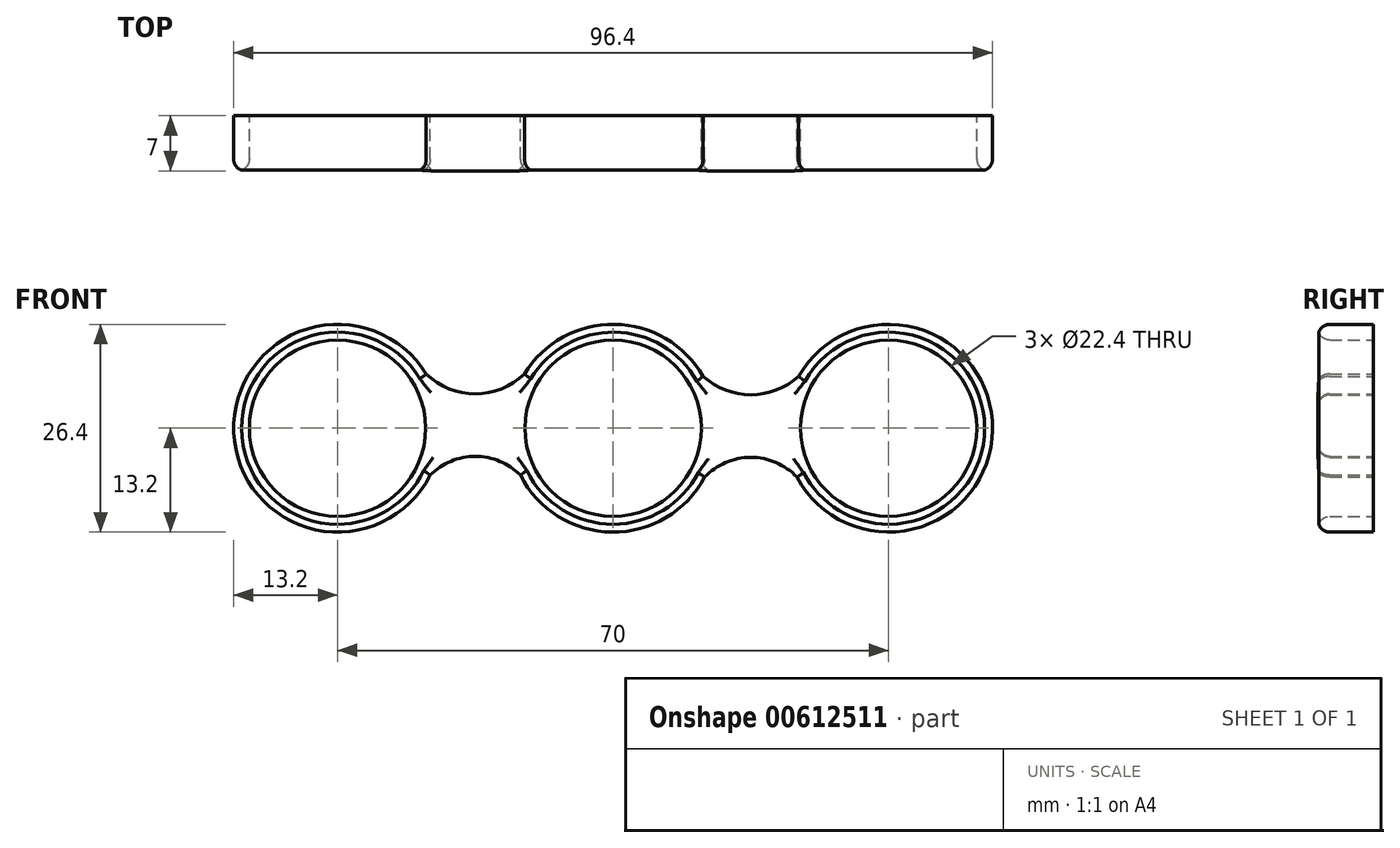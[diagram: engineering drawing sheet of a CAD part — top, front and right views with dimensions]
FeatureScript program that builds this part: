
annotation { "Feature Type Name" : "Feature", "Feature Type Description" : "" }
export const myFeature = defineFeature(function(context is Context, id is Id, definition is map)
    precondition{}
    {
        {
            var Q0;
            Q0=qCreatedBy(makeId("Front.planeOp"),FACE);
            var sketch = newSketch(context, id + "F0", { "sketchPlane" : qUnion([Q0])});
            skCircle(sketch, "E0", {"center": v(0, 0) * mm, "radius": 11.2 * mm});
            skArc(sketch, "E1", {"start": v(-11.77, -5.97) * mm, "mid": v(-0.14, -13.2) * mm, "end": v(11.64, -6.22) * mm});
            skLineSegment(sketch, "E2", {"start": v(11.2, 0) * mm, "end": v(13.2, 0) * mm});
            skArc(sketch, "E3", {"start": v(-23.74, 6.89) * mm, "mid": v(-48.19, -0.52) * mm, "end": v(-23.23, -5.97) * mm});
            skArc(sketch, "E4", {"start": v(23.36, -6.22) * mm, "mid": v(48.2, -0.2) * mm, "end": v(23.56, 6.59) * mm});
            skCircle(sketch, "E5", {"center": v(-35, 0) * mm, "radius": 11.2 * mm});
            skCircle(sketch, "E6", {"center": v(35, 0) * mm, "radius": 11.2 * mm});
            skLineSegment(sketch, "E7", {"start": v(-17.5, 0) * mm, "end": v(-17.5, 13.37) * mm});
            skLineSegment(sketch, "E8", {"start": v(-17.5, 13.37) * mm, "end": v(-17.5, -11.63) * mm});
            skLineSegment(sketch, "E9", {"start": v(17.5, 0) * mm, "end": v(17.5, 13.25) * mm});
            skLineSegment(sketch, "E10", {"start": v(17.5, 13.25) * mm, "end": v(17.5, -11.75) * mm});
            skArc(sketch, "E11", {"start": v(-25.4, 9.06) * mm, "mid": v(-18.87, 4.48) * mm, "end": v(-11.26, 6.89) * mm});
            skArc(sketch, "E12", {"start": v(-11.77, -5.97) * mm, "mid": v(-17.5, -3.58) * mm, "end": v(-23.23, -5.97) * mm});
            skArc(sketch, "E13", {"start": v(11.44, 6.59) * mm, "mid": v(17.5, 4.24) * mm, "end": v(23.56, 6.59) * mm});
            skArc(sketch, "E14", {"start": v(23.36, -6.22) * mm, "mid": v(17.5, -3.7) * mm, "end": v(11.64, -6.22) * mm});
            skLineSegment(sketch, "E15.trimOffspring", {"start": v(21.8, 0) * mm, "end": v(23.8, 0) * mm});
            skArc(sketch, "E16.trimOffspring", {"start": v(11.44, 6.59) * mm, "mid": v(0.17, 13.2) * mm, "end": v(-11.26, 6.89) * mm});
            skSolve(sketch);
        }
        {
            var Q0;
            {var subQ0=sQuery(id+"F0.wireOp",EDGE,"E11");var subQ1=sQuery(id+"F0.wireOp",EDGE,"E3");var subQ2=makeQuery(id+"F0.imprint","INTERSECT",VERTEX,{"disambiguationData":[OD(0.0)],"derivedFrom":[subQ1,subQ0]});Q0=makeQuery(id+"F0.imprint","IMPRINT",FACE,{"disambiguationData":[TD([[makeQuery(id+"F0.imprint","IMPRINT",EDGE,{"disambiguationData":[TD([[subQ2,-1.0]])],"derivedFrom":subQ1}),1.0]])]});}
            var Q1;
            {var subQ5=sQuery(id+"F0.wireOp",EDGE,"E4");Q1=makeQuery(id+"F0.imprint","IMPRINT",FACE,{"disambiguationData":[TD([[makeQuery(id+"F0.imprint","IMPRINT",EDGE,{"derivedFrom":subQ5}),1.0]])]});}
            var Q2;
            Q2=makeQuery(id+"F0.imprint","IMPRINT",FACE,{"disambiguationData":[TD([[makeQuery(id+"F0.imprint","IMPRINT",EDGE,{"derivedFrom":sQuery(id+"F0.wireOp",EDGE,"E0")}),-1.0]])]});
            var Q3;
            Q3=makeQuery(id+"F0.imprint","IMPRINT",FACE,{"disambiguationData":[TD([[makeQuery(id+"F0.imprint","IMPRINT",EDGE,{"derivedFrom":sQuery(id+"F0.wireOp",EDGE,"E5")}),-1.0]])]});
            extrude(context, id + "F1", {"entities" : qUnion([Q0, Q1, Q2, Q3]), "depth" : 7 * mm, "offsetDistance" : 25.4 * mm});
        }
        {
            var Q0;
            Q0=makeQuery(id+"F1.opExtrude","CAP_FACE",FACE,{"disambiguationData":[OSD([sQuery(id+"F0.wireOp",EDGE,"E0"),sQuery(id+"F0.wireOp",EDGE,"E1"),sQuery(id+"F0.wireOp",EDGE,"E3"),sQuery(id+"F0.wireOp",EDGE,"E4"),sQuery(id+"F0.wireOp",EDGE,"E5"),sQuery(id+"F0.wireOp",EDGE,"E6"),sQuery(id+"F0.wireOp",EDGE,"E11"),sQuery(id+"F0.wireOp",EDGE,"E12"),sQuery(id+"F0.wireOp",EDGE,"E13"),sQuery(id+"F0.wireOp",EDGE,"E14"),sQuery(id+"F0.wireOp",EDGE,"E16.trimOffspring")])],"isStart":false});
            fillet(context, id + "F2", {"entities" : qUnion([Q0]), "radius" : 1.5 * mm, "tangentPropagation" : true, "allowEdgeOverflow" : false});
        }
    });
